# Revit family: HVAC-Chilled_Beam-Dadanco-ACB40
name_source: partatom
category: Mechanical Equipment
revit_build: Autodesk Revit 2018 (Build: 20170223_1515(x64)
units: mm (PartAtom-declared; Revit-internal decimal feet)

## family parameters
Always vertical = Yes
Cut with Voids When Loaded = No
OmniClass Number = 23.75.70.17.31
OmniClass Title = Induction Units
Part Type = Normal
Room Calculation Point = No
Round Connector Dimension = Use Diameter
Shared = No
Work Plane-Based = No

## types (1)
- ACB-1
    2 Pipe Coil Configuration = Yes
    2 or 4 pipe = 2
    4 Pipe Coil Configuration = No
    Assembly Code = D3040100
    CWF = 1 GPM
    CWPD = 4.00 ftH2O
    Coil Length = 5' - 4"
    Cooling Primary Air Dry Bulb = 55 °F
    Cooling Primary Air Wet Bulb = 51.3 °F
    Cooling Room Dry Bulb = 75 °F
    Cooling Room Relative Humidity = 50
    Cooling Supply Air Temperature = 62 °F
    Description = Active Chilled Beam
    HWF = 1 GPM
    HWPD = 3.60 ftH2O
    Heating Primary Air Dry Bulb = 55 °F
    Heating Room Dry Bulb = 70 °F
    Heating Supply Air Temperature = 93.4 °F
    Housing Material = Metal-Dadanco-Steel-Galvanized
    Keynote = 23 37 00.A1
    Latent Cooling = 615.0 Btu/h
    Manufacturer = Dadanco
    Model = ACB40
    Net Unit Cooling Sensible = 4728.0 Btu/h
    Net Unit Heating Sensible = 8536.0 Btu/h
    Nominal Unit Length = 6' - 0"
    Nozzle Configuration = 102-TN
    Origin1 = 3' - 0"
    PA = 60 CFM
    PASP = 0.49 in-wg
    Pipe Coil Inlet = 2 Pipe Coi, 0.5 inch SWT Stub Coil Connection
    Pipe Coil Outlet = 2 Pipe Coi, 0.5 inch SWT Stub Coil Connection
    Pipe Material = Metal-Dadanco-Copper-Satin
    Primary Air Inlet Size = 0' - 6"
    Revision Date = 06/24/2020
    SCHW Temp Out = 63.8 °F
    SCHW Temperature = 57 °F
    SHHW Temp Out = 101 °F
    SHHW Temperature = 120 °F
    Secondary Air Sensible Cooling = 3425.0 Btu/h
    Secondary Air Sensible Heating = 9514.0 Btu/h
    Sound Level NC = 15
    Supply Air = 336 CFM
    Total Cooling Capacity = 5343.0 Btu/h
    Type Comments = 2-way Discharge Horizontal Coil
    URL = http://www.dadanco.com
    Unit Height = 0' - 9 3/4"
    Unit Length = 5' - 11 3/4"
    Unit Weight = 88 lb
    Unit Width = 1' - 11 3/4"

## geometry (parser evidence)
native form markers: Sweep x2
no freeform markers — native parametric forms only
